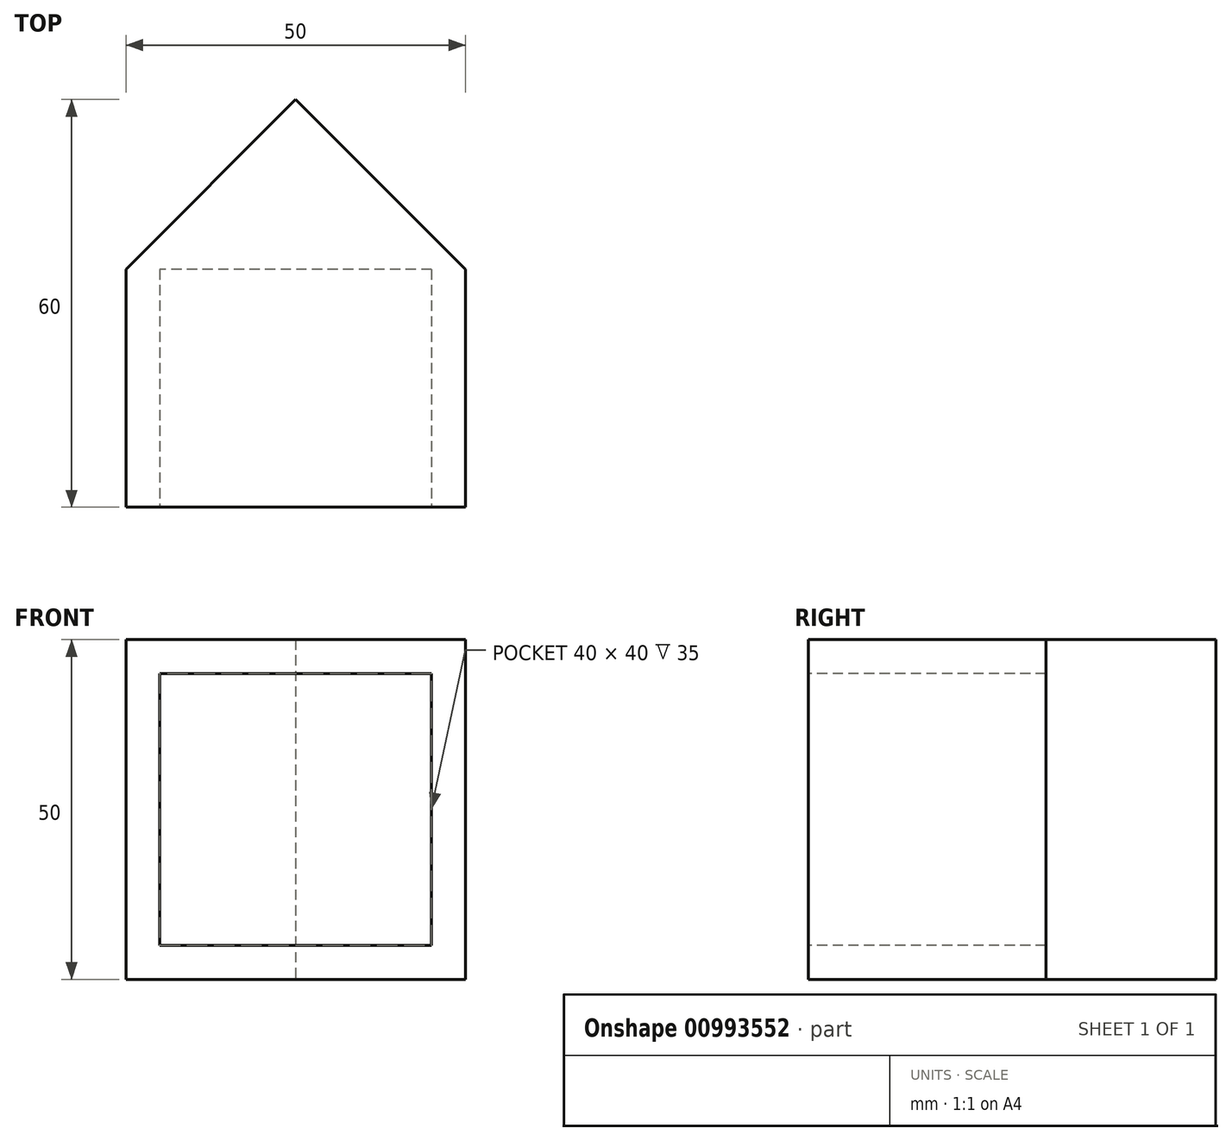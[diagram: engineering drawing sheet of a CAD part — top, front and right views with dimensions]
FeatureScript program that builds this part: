
annotation { "Feature Type Name" : "Feature", "Feature Type Description" : "" }
export const myFeature = defineFeature(function(context is Context, id is Id, definition is map)
    precondition{}
    {
        {
            var Q0;
            Q0=qCreatedBy(makeId("Front.planeOp"),FACE);
            var sketch = newSketch(context, id + "F0", { "sketchPlane" : qUnion([Q0])});
            skLineSegment(sketch, "E0.bottom", {"start": v(0, 0) * mm, "end": v(50, 0) * mm});
            skLineSegment(sketch, "E0.top", {"start": v(0, 50) * mm, "end": v(50, 50) * mm});
            skLineSegment(sketch, "E0.left", {"start": v(0, 0) * mm, "end": v(0, 50) * mm});
            skLineSegment(sketch, "E0.right", {"start": v(50, 0) * mm, "end": v(50, 50) * mm});
            skLineSegment(sketch, "E1.bottom", {"start": v(45, 5) * mm, "end": v(5, 5) * mm});
            skLineSegment(sketch, "E1.top", {"start": v(45, 45) * mm, "end": v(5, 45) * mm});
            skLineSegment(sketch, "E1.left", {"start": v(45, 5) * mm, "end": v(45, 45) * mm});
            skLineSegment(sketch, "E1.right", {"start": v(5, 5) * mm, "end": v(5, 45) * mm});
            skPoint(sketch, "E1.middle", {"position": v(25, 25) * mm});
            skLineSegment(sketch, "E2", {"start": v(25, 25) * mm, "end": v(25, 50) * mm, "construction": true});
            skLineSegment(sketch, "E3", {"start": v(25, 25) * mm, "end": v(0, 25) * mm, "construction": true});
            skSolve(sketch);
        }
        {
            var Q0;
            Q0 = qSketchRegion(id + "F0", true);
            extrude(context, id + "F1", {"entities" : qUnion([Q0]), "oppositeDirection" : true, "depth" : 35 * mm, "offsetDistance" : 25 * mm});
        }
        {
            var Q0;
            Q0=makeQuery(id+"F1.opExtrude","CAP_FACE",FACE,{"disambiguationData":[OSD([sQuery(id+"F0.wireOp",EDGE,"E0.bottom"),sQuery(id+"F0.wireOp",EDGE,"E0.top"),sQuery(id+"F0.wireOp",EDGE,"E0.left"),sQuery(id+"F0.wireOp",EDGE,"E0.right"),sQuery(id+"F0.wireOp",EDGE,"E1.bottom"),sQuery(id+"F0.wireOp",EDGE,"E1.top"),sQuery(id+"F0.wireOp",EDGE,"E1.left"),sQuery(id+"F0.wireOp",EDGE,"E1.right")])],"isStart":false});
            var sketch = newSketch(context, id + "F2", { "sketchPlane" : qUnion([Q0])});
            skLineSegment(sketch, "E4.bottom", {"start": v(0, 50) * mm, "end": v(-50, 50) * mm});
            skLineSegment(sketch, "E4.top", {"start": v(0, 0) * mm, "end": v(-50, 0) * mm});
            skLineSegment(sketch, "E4.left", {"start": v(0, 50) * mm, "end": v(0, 0) * mm});
            skLineSegment(sketch, "E4.right", {"start": v(-50, 50) * mm, "end": v(-50, 0) * mm});
            skSolve(sketch);
        }
        {
            var Q0;
            Q0 = qSketchRegion(id + "F2", true);
            extrude(context, id + "F3", {"entities" : qUnion([Q0]), "operationType" : NewBodyOperationType.ADD, "depth" : 25 * mm, "offsetDistance" : 25 * mm});
        }
        {
            var Q0;
            Q0=makeQuery(id+"F3.opExtrude","CAP_EDGE",EDGE,{"disambiguationData":[OSD([sQuery(id+"F2.wireOp",EDGE,"E4.left")])],"isStart":false});
            var Q1;
            Q1=makeQuery(id+"F3.opExtrude","CAP_EDGE",EDGE,{"disambiguationData":[OSD([sQuery(id+"F2.wireOp",EDGE,"E4.right")])],"isStart":false});
            chamfer(context, id + "F4", {"entities" : qUnion([Q0, Q1]), "width" : 25 * mm, "tangentPropagation" : true});
        }
    });
